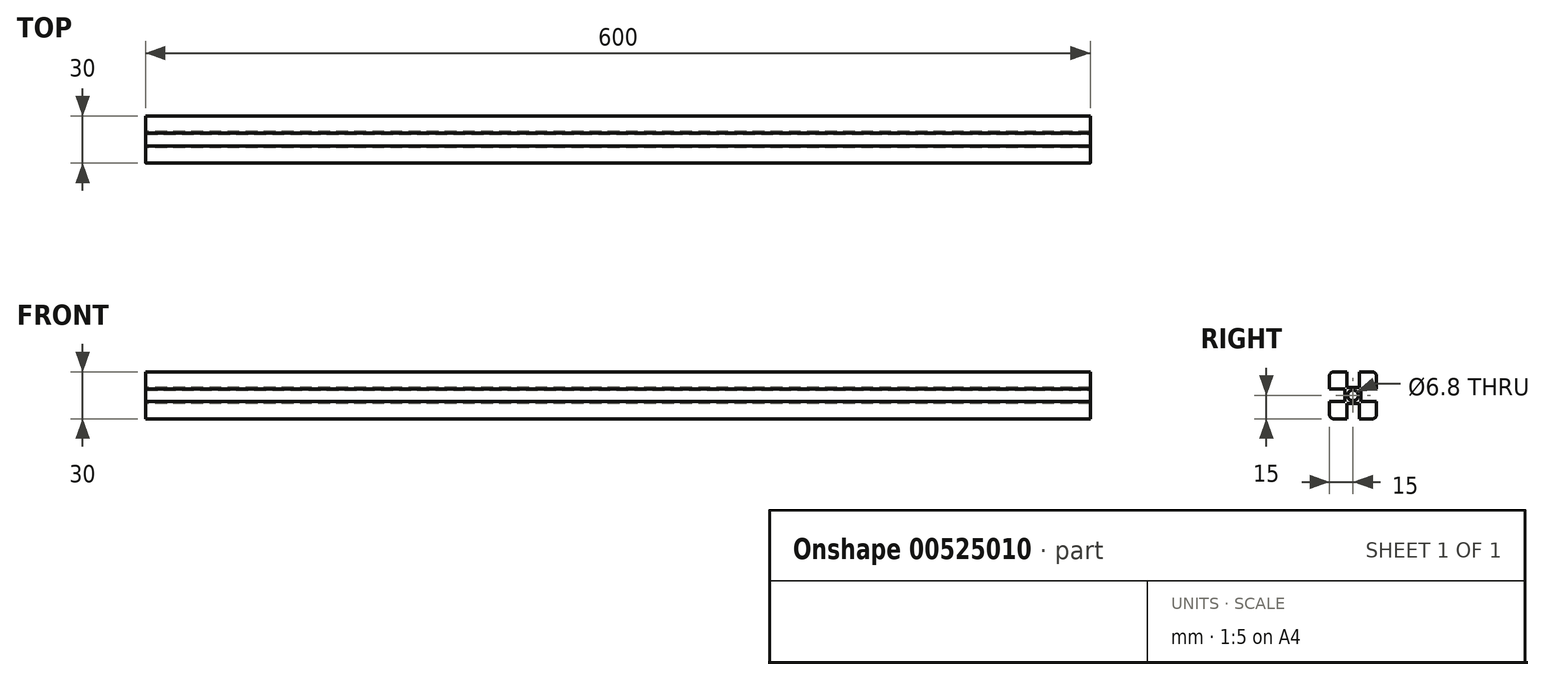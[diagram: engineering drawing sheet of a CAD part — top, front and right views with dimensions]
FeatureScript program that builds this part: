
annotation { "Feature Type Name" : "Feature", "Feature Type Description" : "" }
export const myFeature = defineFeature(function(context is Context, id is Id, definition is map)
    precondition{}
    {
        {
            var Q0;
            Q0=qCreatedBy(makeId("Right.planeOp"),FACE);
            var sketch = newSketch(context, id + "F0", { "sketchPlane" : qUnion([Q0])});
            skLineSegment(sketch, "E0.bottom", {"start": v(15, 15) * mm, "end": v(4, 15) * mm});
            skLineSegment(sketch, "E0.top", {"start": v(15, -15) * mm, "end": v(4, -15) * mm});
            skLineSegment(sketch, "E0.left", {"start": v(15, 15) * mm, "end": v(15, 4) * mm});
            skLineSegment(sketch, "E0.right", {"start": v(-15, 15) * mm, "end": v(-15, 4) * mm});
            skPoint(sketch, "E0.middle", {"position": v(0, 0) * mm});
            skLineSegment(sketch, "E1.top", {"start": v(-4, 5) * mm, "end": v(4, 5) * mm});
            skLineSegment(sketch, "E1.left", {"start": v(-4, 15) * mm, "end": v(-4, 5) * mm});
            skLineSegment(sketch, "E1.right", {"start": v(4, 15) * mm, "end": v(4, 5) * mm});
            skLineSegment(sketch, "E2.bottom", {"start": v(-15, 4) * mm, "end": v(-5, 4) * mm});
            skLineSegment(sketch, "E2.top", {"start": v(-15, -4) * mm, "end": v(-5, -4) * mm});
            skLineSegment(sketch, "E2.right", {"start": v(-5, 4) * mm, "end": v(-5, -4) * mm});
            skLineSegment(sketch, "E3.top", {"start": v(-4, -5) * mm, "end": v(4, -5) * mm});
            skLineSegment(sketch, "E3.left", {"start": v(-4, -15) * mm, "end": v(-4, -5) * mm});
            skLineSegment(sketch, "E3.right", {"start": v(4, -15) * mm, "end": v(4, -5) * mm});
            skLineSegment(sketch, "E4.bottom", {"start": v(15, 4) * mm, "end": v(5, 4) * mm});
            skLineSegment(sketch, "E4.top", {"start": v(15, -4) * mm, "end": v(5, -4) * mm});
            skLineSegment(sketch, "E4.right", {"start": v(5, 4) * mm, "end": v(5, -4) * mm});
            skLineSegment(sketch, "E5.trimOffspring", {"start": v(-4, 15) * mm, "end": v(-15, 15) * mm});
            skLineSegment(sketch, "E6.trimOffspring", {"start": v(15, -4) * mm, "end": v(15, -15) * mm});
            skLineSegment(sketch, "E7.trimOffspring", {"start": v(-4, -15) * mm, "end": v(-15, -15) * mm});
            skLineSegment(sketch, "E8.trimOffspring", {"start": v(-15, -4) * mm, "end": v(-15, -15) * mm});
            skSolve(sketch);
        }
        {
            var Q0;
            Q0 = qSketchRegion(id + "F0", true);
            extrude(context, id + "F1", {"entities" : qUnion([Q0]), "endBound" : BoundingType.SYMMETRIC, "depth" : 600 * mm, "offsetDistance" : 25 * mm});
        }
        {
            var Q0;
            Q0=makeQuery(id+"F1.opExtrude","CAP_FACE",FACE,{"disambiguationData":[OSD([sQuery(id+"F0.wireOp",EDGE,"E0.bottom"),sQuery(id+"F0.wireOp",EDGE,"E0.top"),sQuery(id+"F0.wireOp",EDGE,"E0.left"),sQuery(id+"F0.wireOp",EDGE,"E0.right"),sQuery(id+"F0.wireOp",EDGE,"E1.top"),sQuery(id+"F0.wireOp",EDGE,"E1.left"),sQuery(id+"F0.wireOp",EDGE,"E1.right"),sQuery(id+"F0.wireOp",EDGE,"E2.bottom"),sQuery(id+"F0.wireOp",EDGE,"E2.top"),sQuery(id+"F0.wireOp",EDGE,"E2.right"),sQuery(id+"F0.wireOp",EDGE,"E3.top"),sQuery(id+"F0.wireOp",EDGE,"E3.left"),sQuery(id+"F0.wireOp",EDGE,"E3.right"),sQuery(id+"F0.wireOp",EDGE,"E4.bottom"),sQuery(id+"F0.wireOp",EDGE,"E4.top"),sQuery(id+"F0.wireOp",EDGE,"E4.right"),sQuery(id+"F0.wireOp",EDGE,"E5.trimOffspring"),sQuery(id+"F0.wireOp",EDGE,"E6.trimOffspring"),sQuery(id+"F0.wireOp",EDGE,"E7.trimOffspring"),sQuery(id+"F0.wireOp",EDGE,"E8.trimOffspring")])],"isStart":false});
            var sketch = newSketch(context, id + "F2", { "sketchPlane" : qUnion([Q0])});
            skCircle(sketch, "E9", {"center": v(0, 0) * mm, "radius": 3.4 * mm});
            skSolve(sketch);
        }
        {
            var Q0;
            Q0 = qSketchRegion(id + "F2", true);
            extrude(context, id + "F3", {"entities" : qUnion([Q0]), "operationType" : NewBodyOperationType.REMOVE, "oppositeDirection" : true, "depth" : 600 * mm, "offsetDistance" : 25 * mm});
        }
        {
            var Q0;
            Q0=makeQuery(id+"F1.opExtrude","SWEPT_EDGE",EDGE,{"disambiguationData":[OSD([sQuery(id+"F0.wireOp",EDGE,"E0.top"),sQuery(id+"F0.wireOp",EDGE,"E6.trimOffspring")])]});
            var Q1;
            Q1=makeQuery(id+"F1.opExtrude","SWEPT_EDGE",EDGE,{"disambiguationData":[OSD([sQuery(id+"F0.wireOp",EDGE,"E0.bottom"),sQuery(id+"F0.wireOp",EDGE,"E0.left")])]});
            var Q2;
            Q2=makeQuery(id+"F1.opExtrude","SWEPT_EDGE",EDGE,{"disambiguationData":[OSD([sQuery(id+"F0.wireOp",EDGE,"E7.trimOffspring"),sQuery(id+"F0.wireOp",EDGE,"E8.trimOffspring")])]});
            var Q3;
            Q3=makeQuery(id+"F1.opExtrude","SWEPT_EDGE",EDGE,{"disambiguationData":[OSD([sQuery(id+"F0.wireOp",EDGE,"E0.right"),sQuery(id+"F0.wireOp",EDGE,"E5.trimOffspring")])]});
            fillet(context, id + "F4", {"entities" : qUnion([Q0, Q1, Q2, Q3]), "radius" : 3 * mm, "tangentPropagation" : true, "allowEdgeOverflow" : false});
        }
    });
